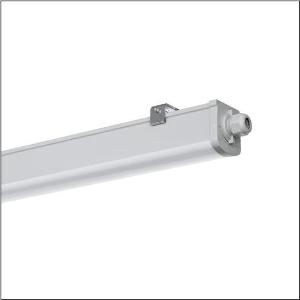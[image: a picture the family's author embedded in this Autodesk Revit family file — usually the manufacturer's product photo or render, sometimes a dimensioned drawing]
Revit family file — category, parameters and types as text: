
# Revit family: monsun_r__31_51fa20dk430b_aae0
name_source: partatom
category: Lighting Fixtures
units: mm (PartAtom-declared; Revit-internal decimal feet)

## family parameters
Cut with Voids When Loaded = No
Host = Face
Light Source = No
Part Type = Normal
Room Calculation Point = No
Round Connector Dimension = Use Diameter
Shared = No

## types (1)
- Monsun® 31 (1 x LED, 3000 lm, 22 W, 4000K)
    Apparent Load = 22 VA
    CIE Flux Codes = 42 72 91 92 100
    Color Rendering = 80
    Color Temperature = 4000K
    Default Elevation = 1800 mm
    Description = Monsun® 31, damp-proof luminaire, primary optical cover: diffuser, of PC, frosted, light emission: direct distribution, primary light characteristic: symmetric, installation type: surface-mounted, LED, rated luminous flux: 3.000lm, luminous efficacy: 136lm/W, light colour: 840, colour temperature: 4000K, control gear: ECG, with terminal, 5+1-pole, max. 2.5mm², through-wiring: 3x 2.5mm² + 3x 1.5mm², mains connection: 220..240V, AC, 50/60Hz, rated input power: 22W, housing, luminaire housing, of PC, light grey (RAL 7035), length: 1.158mm, width: 68mm, height: 76mm, protection rating (complete): IP66, insulation class (complete): insulation class II (safety insulation), certification: CE, ENEC, UKCA, protection symbol: D, impact resistance: IK08, permissible operating ambient temperature: -20..+40°C, corresponds to IFS (International Featured Standards) requirements for safety and quality in the food industry, contact your sales advisor before using the luminaires in applications with unclear chemical exposure, large temperature fluctuations or condensation-forming humidity, packaging unit: 1 piece
    Height = 77 mm
    Lamp = 1 x LED
    Lamp Light Flux = 3000 lm
    Lamp Power = 22 W
    Lamp count = 1
    Length = 1218 mm
    Luminous efficacy = 136 lm/W
    Manufacturer = Siteco
    ModVariant = No
    Model = 51FA20DK430B
    Mounting Place = Ceiling
    Mounting Type = Surface mounted
    Number of Poles = 1
    OnlyDefault = Yes
    Power Factor = 1
    Product Name = Monsun® 31
    Product group = damp-proof luminaire
    ProductGroupID = 301
    Protection Class = Protection class II
    Protection Degree = IP 66
    RLX_Detail_Level = 1
    RLX_Emergency_Light_Flux = 0 lm
    RLX_Emergency_Type = 0
    RLX_Emergency_Type_DB = No
    RlxData = <blob elided: 32973 chars, md5=fce63b54>
    Socket = socket
    Standby Power = 0 W
    System Light Flux = 3000 lm
    System Power = 22 W
    Type Comments = Product without accessories
    Type Image = l_1006174.jpg
    URL = http://relux.com
    VarID = ---
    Voltage = 0 V
    Weight = 0.00 kg
    Width = 69 mm

## geometry (parser evidence)
native form markers: Blend x4, Sweep x13
no freeform markers — native parametric forms only
